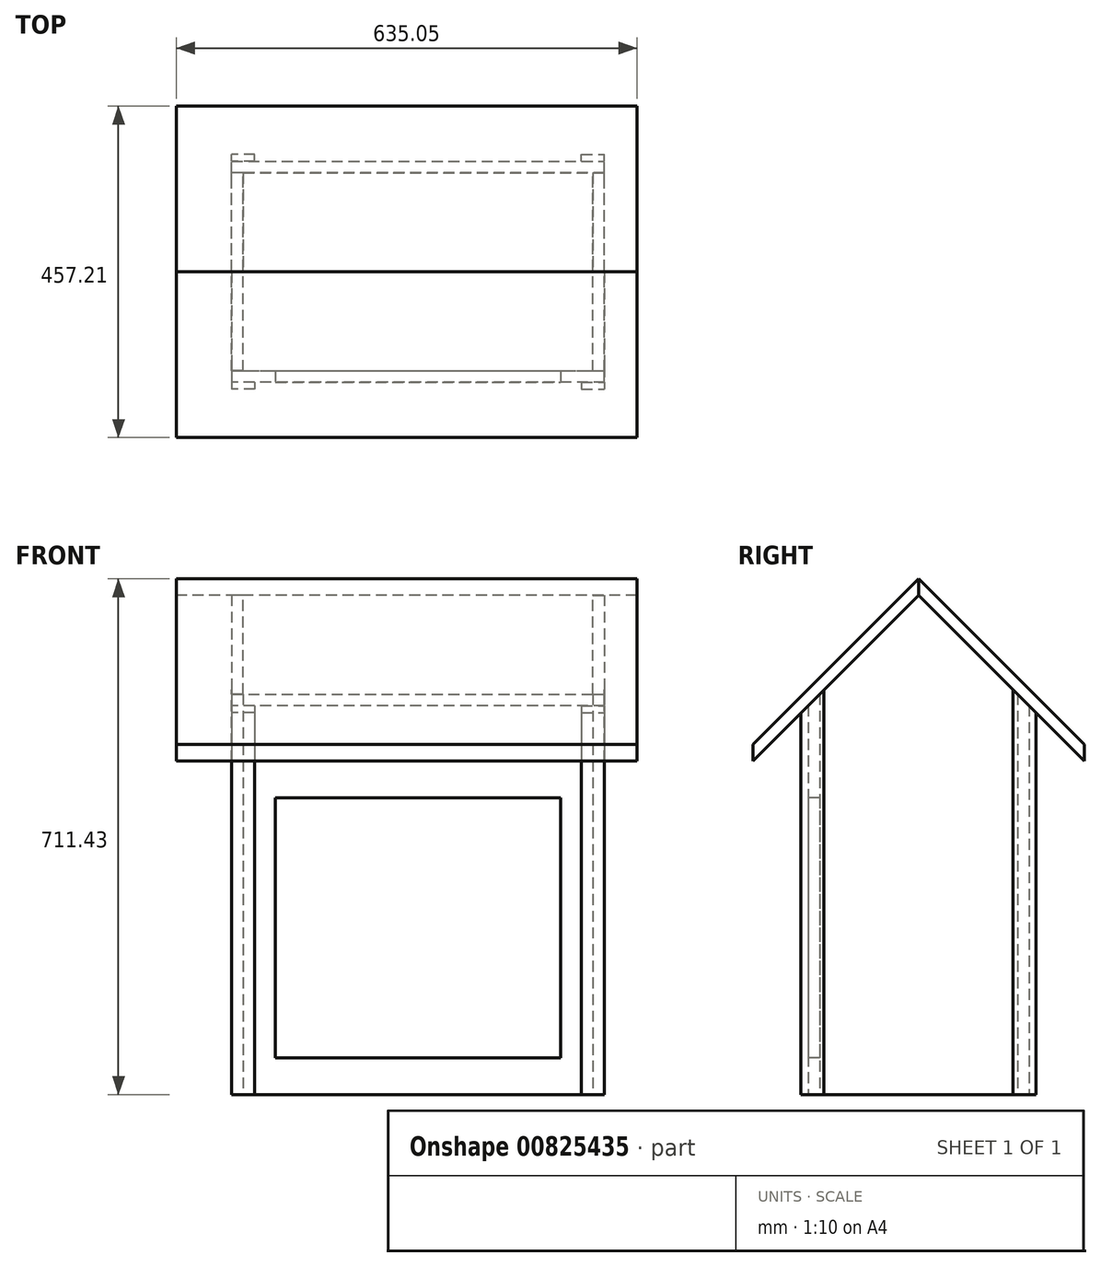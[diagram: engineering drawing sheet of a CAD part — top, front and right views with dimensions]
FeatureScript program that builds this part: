
annotation { "Feature Type Name" : "Feature", "Feature Type Description" : "" }
export const myFeature = defineFeature(function(context is Context, id is Id, definition is map)
    precondition{}
    {
        {
            assignVariable(context, id + "F0", {"name" : "depth", "anyValue" : 273.05 * mm});
        }
        {
            assignVariable(context, id + "F1", {"name" : "width", "anyValue" : 482.6 * mm});
        }
        {
            assignVariable(context, id + "F2", {"name" : "thickness", "anyValue" : 5 / 203.2 * mm});
        }
        {
            assignVariable(context, id + "F3", {"name" : "height", "anyValue" : 688.97 * mm});
        }
        {
            var Q0;
            Q0=qCreatedBy(makeId("Top.planeOp"),FACE);
            var sketch = newSketch(context, id + "F4", { "sketchPlane" : qUnion([Q0])});
            skLineSegment(sketch, "E0.bottom", {"start": v(0, 0) * mm, "end": v(482.6, 0) * mm});
            skLineSegment(sketch, "E0.top", {"start": v(0, 273.05) * mm, "end": v(482.6, 273.05) * mm});
            skLineSegment(sketch, "E0.left", {"start": v(0, 0) * mm, "end": v(0, 273.05) * mm});
            skLineSegment(sketch, "E0.right", {"start": v(482.6, 0) * mm, "end": v(482.6, 273.05) * mm});
            skSolve(sketch);
        }
        {
            var Q0;
            Q0=qSketchRegion(id+"F4",true);
            extrude(context, id + "F5", {"entities" : qUnion([Q0]), "depth" : getVariable(context, 'thickness'), "offsetDistance" : 25.4 * mm});
        }
        {
            var Q0;
            Q0=makeQuery(id+"F5.opExtrude","CAP_FACE",FACE,{"disambiguationData":[OSD([sQuery(id+"F4.wireOp",EDGE,"E0.bottom"),sQuery(id+"F4.wireOp",EDGE,"E0.top"),sQuery(id+"F4.wireOp",EDGE,"E0.left"),sQuery(id+"F4.wireOp",EDGE,"E0.right")])],"isStart":true});
            var sketch = newSketch(context, id + "F6", { "sketchPlane" : qUnion([Q0])});
            skLineSegment(sketch, "E1.bottom", {"start": v(0, 0) * mm, "end": v(-15.88, 0) * mm});
            skLineSegment(sketch, "E1.top", {"start": v(0, -273.05) * mm, "end": v(-15.87, -273.05) * mm});
            skLineSegment(sketch, "E1.left", {"start": v(0, 0) * mm, "end": v(0, -273.05) * mm});
            skLineSegment(sketch, "E1.right", {"start": v(-15.88, 0) * mm, "end": v(-15.88, -273.05) * mm});
            skSolve(sketch);
        }
        {
            var Q0;
            Q0=makeQuery(id+"F6.imprint","IMPRINT",FACE,{"disambiguationData":[TD([[makeQuery(id+"F6.imprint","IMPRINT",EDGE,{"derivedFrom":sQuery(id+"F6.wireOp",EDGE,"E1.bottom")}),1.0]])]});
            extrude(context, id + "F7", {"entities" : qUnion([Q0]), "oppositeDirection" : true, "depth" : getVariable(context, 'height'), "offsetDistance" : 25.4 * mm});
        }
        {
            var Q0;
            Q0=makeQuery(id+"F7.opExtrude","SWEPT_FACE",FACE,{"disambiguationData":[OSD([sQuery(id+"F6.wireOp",EDGE,"E1.right")])]});
            var sketch = newSketch(context, id + "F8", { "sketchPlane" : qUnion([Q0])});
            skLineSegment(sketch, "E2", {"start": v(-136.53, 688.98) * mm, "end": v(-273.05, 552.45) * mm});
            skLineSegment(sketch, "E3", {"start": v(-273.05, 552.45) * mm, "end": v(-273.05, 688.98) * mm});
            skLineSegment(sketch, "E4", {"start": v(-273.05, 688.98) * mm, "end": v(-136.53, 688.98) * mm});
            skLineSegment(sketch, "E5", {"start": v(-136.53, 688.98) * mm, "end": v(-136.53, 0) * mm, "construction": true});
            skLineSegment(sketch, "E6.MirrorCS", {"start": v(0, 688.98) * mm, "end": v(-136.53, 688.98) * mm});
            skLineSegment(sketch, "E7.MirrorCS", {"start": v(0, 552.45) * mm, "end": v(0, 688.98) * mm});
            skLineSegment(sketch, "E8.MirrorCS", {"start": v(-136.53, 688.98) * mm, "end": v(0, 552.45) * mm});
            skSolve(sketch);
        }
        {
            var Q0;
            Q0=qSketchRegion(id+"F8",true);
            extrude(context, id + "F9", {"entities" : qUnion([Q0]), "operationType" : NewBodyOperationType.REMOVE, "endBound" : BoundingType.UP_TO_NEXT, "oppositeDirection" : true, "depth" : 25.4 * mm, "offsetDistance" : 25.4 * mm});
        }
        {
            var Q0;
            Q0=qCreatedBy(makeId("Right.planeOp"),FACE);
            cPlane(context, id + "F10", {"entities" : qUnion([Q0]), "cplaneType" : CPlaneType.OFFSET, "offset" : getVariable(context, 'width') / 2, "width" : 152.4 * mm, "height" : 152.4 * mm});
        }
        {
            var Q0;
            Q0=makeQuery(id+"F7.opExtrude","SWEPT_BODY",BODY,{"disambiguationData":[OSD([sQuery(id+"F6.wireOp",EDGE,"E1.bottom"),sQuery(id+"F6.wireOp",EDGE,"E1.top"),sQuery(id+"F6.wireOp",EDGE,"E1.left"),sQuery(id+"F6.wireOp",EDGE,"E1.right")])]});
            var Q1;
            Q1=qCreatedBy(id+"F10.planeOp",FACE);
            mirror(context, id + "F11", {"entities" : qUnion([Q0]), "mirrorPlane" : qUnion([Q1])});
        }
        {
            var Q0;
            Q0=makeQuery(id+"F5.opExtrude","CAP_FACE",FACE,{"disambiguationData":[OSD([sQuery(id+"F4.wireOp",EDGE,"E0.bottom"),sQuery(id+"F4.wireOp",EDGE,"E0.top"),sQuery(id+"F4.wireOp",EDGE,"E0.left"),sQuery(id+"F4.wireOp",EDGE,"E0.right")])],"isStart":true});
            var sketch = newSketch(context, id + "F12", { "sketchPlane" : qUnion([Q0])});
            skLineSegment(sketch, "E9.bottom", {"start": v(498.48, -273.05) * mm, "end": v(-15.87, -273.05) * mm});
            skLineSegment(sketch, "E9.top", {"start": v(498.48, -288.93) * mm, "end": v(-15.87, -288.93) * mm});
            skLineSegment(sketch, "E9.left", {"start": v(498.48, -273.05) * mm, "end": v(498.48, -288.93) * mm});
            skLineSegment(sketch, "E9.right", {"start": v(-15.88, -273.05) * mm, "end": v(-15.87, -288.93) * mm});
            skSolve(sketch);
        }
        {
            var Q0;
            Q0=qSketchRegion(id+"F12",true);
            extrude(context, id + "F13", {"entities" : qUnion([Q0]), "oppositeDirection" : true, "depth" : (getVariable(context, 'height') - getVariable(context, 'depth') / 2), "offsetDistance" : 25.4 * mm});
        }
        {
            var Q0;
            Q0=makeQuery(id+"F13.opExtrude","SWEPT_FACE",FACE,{"disambiguationData":[OSD([sQuery(id+"F12.wireOp",EDGE,"E9.left")])]});
            var sketch = newSketch(context, id + "F14", { "sketchPlane" : qUnion([Q0])});
            skLineSegment(sketch, "E10", {"start": v(273.05, 552.45) * mm, "end": v(288.93, 536.58) * mm});
            skLineSegment(sketch, "E11", {"start": v(288.93, 536.58) * mm, "end": v(288.93, 552.45) * mm});
            skLineSegment(sketch, "E12", {"start": v(288.93, 552.45) * mm, "end": v(273.05, 552.45) * mm});
            skSolve(sketch);
        }
        {
            var Q0;
            Q0=makeQuery(id+"F14.imprint","IMPRINT",FACE,{"disambiguationData":[TD([[makeQuery(id+"F14.imprint","IMPRINT",EDGE,{"derivedFrom":sQuery(id+"F14.wireOp",EDGE,"E10")}),1.0]])]});
            extrude(context, id + "F15", {"entities" : qUnion([Q0]), "operationType" : NewBodyOperationType.REMOVE, "endBound" : BoundingType.UP_TO_NEXT, "oppositeDirection" : true, "depth" : 25.4 * mm, "offsetDistance" : 25.4 * mm});
        }
        {
            var Q0;
            Q0=makeQuery(id+"F5.opExtrude","CAP_FACE",FACE,{"disambiguationData":[OSD([sQuery(id+"F4.wireOp",EDGE,"E0.bottom"),sQuery(id+"F4.wireOp",EDGE,"E0.top"),sQuery(id+"F4.wireOp",EDGE,"E0.left"),sQuery(id+"F4.wireOp",EDGE,"E0.right")])],"isStart":true});
            var sketch = newSketch(context, id + "F16", { "sketchPlane" : qUnion([Q0])});
            skLineSegment(sketch, "E13.bottom", {"start": v(-15.88, 15.87) * mm, "end": v(498.48, 15.87) * mm});
            skLineSegment(sketch, "E13.top", {"start": v(-15.87, 0) * mm, "end": v(498.48, 0) * mm});
            skLineSegment(sketch, "E13.left", {"start": v(-15.88, 15.87) * mm, "end": v(-15.88, 0) * mm});
            skLineSegment(sketch, "E13.right", {"start": v(498.48, 15.87) * mm, "end": v(498.48, 0) * mm});
            skSolve(sketch);
        }
        {
            var Q0;
            Q0=qSketchRegion(id+"F16",true);
            extrude(context, id + "F17", {"entities" : qUnion([Q0]), "oppositeDirection" : true, "depth" : getVariable(context, 'height') - getVariable(context, 'depth') / 2, "offsetDistance" : 25.4 * mm});
        }
        {
            var Q0;
            Q0=makeQuery(id+"F17.opExtrude","SWEPT_FACE",FACE,{"disambiguationData":[OSD([sQuery(id+"F16.wireOp",EDGE,"E13.left")])]});
            var sketch = newSketch(context, id + "F18", { "sketchPlane" : qUnion([Q0])});
            skLineSegment(sketch, "E14", {"start": v(0, 552.45) * mm, "end": v(15.87, 536.58) * mm});
            skLineSegment(sketch, "E15", {"start": v(15.87, 536.58) * mm, "end": v(15.87, 552.45) * mm});
            skLineSegment(sketch, "E16", {"start": v(15.87, 552.45) * mm, "end": v(0, 552.45) * mm});
            skSolve(sketch);
        }
        {
            var Q0;
            Q0=makeQuery(id+"F18.imprint","IMPRINT",FACE,{"disambiguationData":[TD([[makeQuery(id+"F18.imprint","IMPRINT",EDGE,{"derivedFrom":sQuery(id+"F18.wireOp",EDGE,"E14")}),1.0]])]});
            extrude(context, id + "F19", {"entities" : qUnion([Q0]), "operationType" : NewBodyOperationType.REMOVE, "endBound" : BoundingType.UP_TO_NEXT, "oppositeDirection" : true, "depth" : 25.4 * mm, "offsetDistance" : 25.4 * mm});
        }
        {
            var Q0;
            Q0=makeQuery(id+"F17.opExtrude","SWEPT_FACE",FACE,{"disambiguationData":[OSD([sQuery(id+"F16.wireOp",EDGE,"E13.bottom")])]});
            var sketch = newSketch(context, id + "F20", { "sketchPlane" : qUnion([Q0])});
            skLineSegment(sketch, "E17.bottom", {"start": v(44.45, 409.58) * mm, "end": v(438.15, 409.58) * mm});
            skLineSegment(sketch, "E17.top", {"start": v(44.45, 50.8) * mm, "end": v(438.15, 50.8) * mm});
            skLineSegment(sketch, "E17.left", {"start": v(44.45, 409.57) * mm, "end": v(44.45, 50.8) * mm});
            skLineSegment(sketch, "E17.right", {"start": v(438.15, 409.58) * mm, "end": v(438.15, 50.8) * mm});
            skLineSegment(sketch, "E18", {"start": v(241.3, 536.58) * mm, "end": v(241.3, 0) * mm, "construction": true});
            skPoint(sketch, "E18.startSnap0", {"position": v(241.3, 0) * mm});
            skPoint(sketch, "E19", {"position": v(241.3, 409.58) * mm});
            skSolve(sketch);
        }
        {
            var Q0;
            Q0=qSketchRegion(id+"F20",true);
            extrude(context, id + "F21", {"entities" : qUnion([Q0]), "operationType" : NewBodyOperationType.REMOVE, "endBound" : BoundingType.UP_TO_NEXT, "oppositeDirection" : true, "depth" : 25.4 * mm, "offsetDistance" : 25.4 * mm});
        }
        {
            var Q0;
            Q0=makeQuery(id+"F7.opExtrude","SWEPT_FACE",FACE,{"disambiguationData":[OSD([sQuery(id+"F6.wireOp",EDGE,"E1.right")])]});
            var sketch = newSketch(context, id + "F22", { "sketchPlane" : qUnion([Q0])});
            skLineSegment(sketch, "E20", {"start": v(-136.53, 688.98) * mm, "end": v(-136.53, 711.43) * mm});
            skLineSegment(sketch, "E21", {"start": v(-136.53, 711.43) * mm, "end": v(92.08, 482.83) * mm});
            skLineSegment(sketch, "E22", {"start": v(92.07, 482.83) * mm, "end": v(92.07, 460.38) * mm});
            skLineSegment(sketch, "E23", {"start": v(92.07, 460.38) * mm, "end": v(-136.53, 688.98) * mm});
            skSolve(sketch);
        }
        {
            var Q0;
            Q0=qSketchRegion(id+"F22",true);
            extrude(context, id + "F23", {"entities" : qUnion([Q0]), "oppositeDirection" : true, "depth" : getVariable(context, 'width') + getVariable(context, 'thickness') * 2 + 76.2 * mm, "offsetDistance" : 25.4 * mm, "hasSecondDirection" : true, "secondDirectionOppositeDirection" : false, "secondDirectionDepth" : 76.2 * mm});
        }
        {
            var Q0;
            Q0=qCreatedBy(makeId("Front.planeOp"),FACE);
            cPlane(context, id + "F24", {"entities" : qUnion([Q0]), "cplaneType" : CPlaneType.OFFSET, "offset" : (getVariable(context, 'depth') / 2), "oppositeDirection" : true, "width" : 152.4 * mm, "height" : 152.4 * mm});
        }
        {
            var Q0;
            Q0=makeQuery(id+"F23.opExtrude","SWEPT_BODY",BODY,{"disambiguationData":[OSD([sQuery(id+"F22.wireOp",EDGE,"E20"),sQuery(id+"F22.wireOp",EDGE,"E21"),sQuery(id+"F22.wireOp",EDGE,"E22"),sQuery(id+"F22.wireOp",EDGE,"E23")])]});
            var Q1;
            Q1=qCreatedBy(id+"F24.planeOp",FACE);
            mirror(context, id + "F25", {"entities" : qUnion([Q0]), "mirrorPlane" : qUnion([Q1])});
        }
        {
            assignVariable(context, id + "F26", {"name" : "trim_thickness", "anyValue" : 3 / 203.2 * mm});
        }
        {
            var Q0;
            Q0=makeQuery(id+"F17.opExtrude","SWEPT_FACE",FACE,{"disambiguationData":[OSD([sQuery(id+"F16.wireOp",EDGE,"E13.left")])]});
            var sketch = newSketch(context, id + "F27", { "sketchPlane" : qUnion([Q0])});
            skLineSegment(sketch, "E24", {"start": v(-6.35, 558.8) * mm, "end": v(25.4, 527.05) * mm});
            skLineSegment(sketch, "E25", {"start": v(25.4, 527.05) * mm, "end": v(25.4, 0) * mm});
            skLineSegment(sketch, "E26", {"start": v(25.4, 0) * mm, "end": v(-6.35, 0) * mm});
            skLineSegment(sketch, "E27", {"start": v(-6.35, 0) * mm, "end": v(-6.35, 558.8) * mm});
            skSolve(sketch);
        }
        {
            var Q0;
            Q0=qSketchRegion(id+"F27",true);
            extrude(context, id + "F28", {"entities" : qUnion([Q0]), "depth" : getVariable(context, 'trim_thickness'), "offsetDistance" : 25.4 * mm});
        }
        {
            var Q0;
            Q0=makeQuery(id+"F28.opExtrude","CAP_FACE",FACE,{"disambiguationData":[OSD([sQuery(id+"F27.wireOp",EDGE,"E24"),sQuery(id+"F27.wireOp",EDGE,"E25"),sQuery(id+"F27.wireOp",EDGE,"E26"),sQuery(id+"F27.wireOp",EDGE,"E27")])],"isStart":true});
            var sketch = newSketch(context, id + "F29", { "sketchPlane" : qUnion([Q0])});
            skLineSegment(sketch, "E28.0", {"start": v(-25.4, 527.05) * mm, "end": v(-25.4, 0) * mm});
            skLineSegment(sketch, "E29.0", {"start": v(-15.87, 536.58) * mm, "end": v(-15.87, 0) * mm});
            skLineSegment(sketch, "E30", {"start": v(-25.4, 527.05) * mm, "end": v(-15.87, 536.58) * mm});
            skLineSegment(sketch, "E31", {"start": v(-25.4, 0) * mm, "end": v(-15.87, 0) * mm});
            skSolve(sketch);
        }
        {
            var Q0;
            Q0=qSketchRegion(id+"F29",true);
            extrude(context, id + "F30", {"entities" : qUnion([Q0]), "depth" : 31.75 * mm - getVariable(context, 'trim_thickness'), "offsetDistance" : 25.4 * mm});
        }
        {
            var Q0;
            Q0=makeQuery(id+"F30.opExtrude","SWEPT_BODY",BODY,{"disambiguationData":[OSD([sQuery(id+"F29.wireOp",EDGE,"E28.0"),sQuery(id+"F29.wireOp",EDGE,"E29.0"),sQuery(id+"F29.wireOp",EDGE,"E30"),sQuery(id+"F29.wireOp",EDGE,"E31")])]});
            var Q1;
            Q1=makeQuery(id+"F28.opExtrude","SWEPT_BODY",BODY,{"disambiguationData":[OSD([sQuery(id+"F27.wireOp",EDGE,"E24"),sQuery(id+"F27.wireOp",EDGE,"E25"),sQuery(id+"F27.wireOp",EDGE,"E26"),sQuery(id+"F27.wireOp",EDGE,"E27")])]});
            var Q2;
            Q2=qCreatedBy(id+"F24.planeOp",FACE);
            mirror(context, id + "F31", {"entities" : qUnion([Q0, Q1]), "mirrorPlane" : qUnion([Q2])});
        }
        {
            var Q0;
            Q0=makeQuery(id+"F28.opExtrude","SWEPT_BODY",BODY,{"disambiguationData":[OSD([sQuery(id+"F27.wireOp",EDGE,"E24"),sQuery(id+"F27.wireOp",EDGE,"E25"),sQuery(id+"F27.wireOp",EDGE,"E26"),sQuery(id+"F27.wireOp",EDGE,"E27")])]});
            var Q1;
            Q1=makeQuery(id+"F30.opExtrude","SWEPT_BODY",BODY,{"disambiguationData":[OSD([sQuery(id+"F29.wireOp",EDGE,"E28.0"),sQuery(id+"F29.wireOp",EDGE,"E29.0"),sQuery(id+"F29.wireOp",EDGE,"E30"),sQuery(id+"F29.wireOp",EDGE,"E31")])]});
            var Q2;
            Q2=makeQuery(id+"F31.opPattern","COPY",BODY,{"derivedFrom":makeQuery(id+"F28.opExtrude","SWEPT_BODY",BODY,{"disambiguationData":[OSD([sQuery(id+"F27.wireOp",EDGE,"E24"),sQuery(id+"F27.wireOp",EDGE,"E25"),sQuery(id+"F27.wireOp",EDGE,"E26"),sQuery(id+"F27.wireOp",EDGE,"E27")])]}),"instanceName":"1"});
            var Q3;
            Q3=makeQuery(id+"F31.opPattern","COPY",BODY,{"derivedFrom":makeQuery(id+"F30.opExtrude","SWEPT_BODY",BODY,{"disambiguationData":[OSD([sQuery(id+"F29.wireOp",EDGE,"E28.0"),sQuery(id+"F29.wireOp",EDGE,"E29.0"),sQuery(id+"F29.wireOp",EDGE,"E30"),sQuery(id+"F29.wireOp",EDGE,"E31")])]}),"instanceName":"1"});
            var Q4;
            Q4=qCreatedBy(id+"F10.planeOp",FACE);
            mirror(context, id + "F32", {"entities" : qUnion([Q0, Q1, Q2, Q3]), "mirrorPlane" : qUnion([Q4])});
        }
    });
